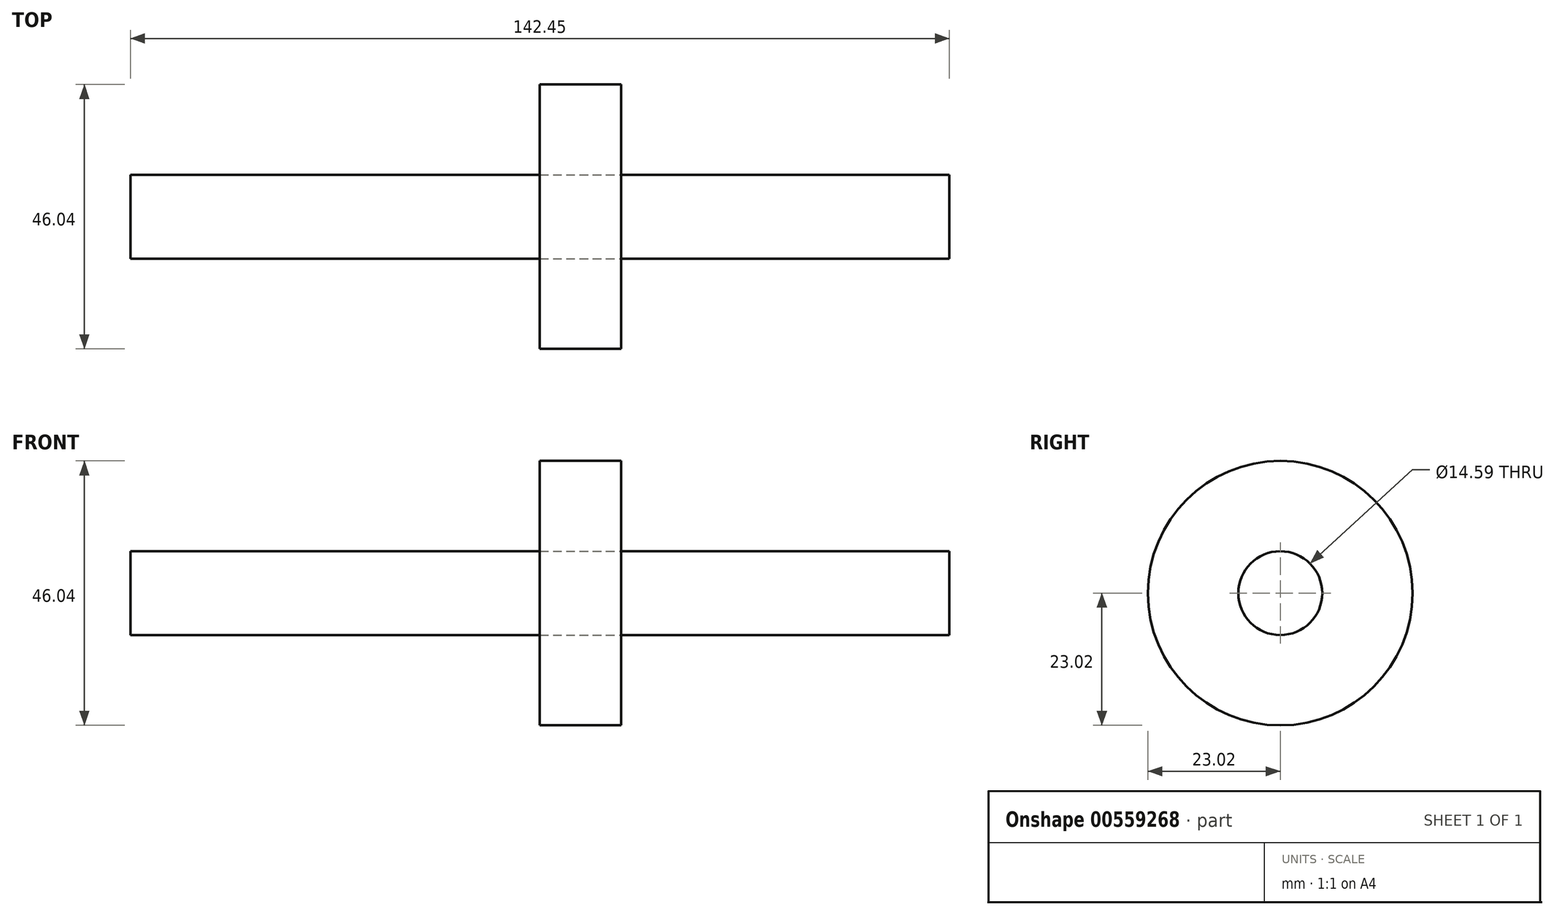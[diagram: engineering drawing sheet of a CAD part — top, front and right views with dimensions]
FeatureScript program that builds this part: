
annotation { "Feature Type Name" : "Feature", "Feature Type Description" : "" }
export const myFeature = defineFeature(function(context is Context, id is Id, definition is map)
    precondition{}
    {
        {
            var Q0;
            Q0=qCreatedBy(makeId("Front.planeOp"),FACE);
            var sketch = newSketch(context, id + "F0", { "sketchPlane" : qUnion([Q0])});
            skLineSegment(sketch, "E0.bottom", {"start": v(70.7, 7.3) * mm, "end": v(-71.75, 7.3) * mm});
            skLineSegment(sketch, "E0.top", {"start": v(70.7, 0) * mm, "end": v(-71.75, 0) * mm});
            skLineSegment(sketch, "E0.left", {"start": v(70.7, 7.3) * mm, "end": v(70.7, 0) * mm});
            skLineSegment(sketch, "E0.right", {"start": v(-71.75, 7.3) * mm, "end": v(-71.75, 0) * mm});
            skLineSegment(sketch, "E1.bottom", {"start": v(13.61, 23.02) * mm, "end": v(-0.52, 23.02) * mm});
            skLineSegment(sketch, "E1.top", {"start": v(13.61, 7.3) * mm, "end": v(-0.52, 7.3) * mm});
            skLineSegment(sketch, "E1.left", {"start": v(13.61, 23.02) * mm, "end": v(13.61, 7.3) * mm});
            skLineSegment(sketch, "E1.right", {"start": v(-0.52, 23.02) * mm, "end": v(-0.52, 7.3) * mm});
            skSolve(sketch);
        }
        {
            var Q0;
            Q0=makeQuery(id+"F0.imprint","IMPRINT",FACE,{"disambiguationData":[TD([[makeQuery(id+"F0.imprint","IMPRINT",EDGE,{"derivedFrom":sQuery(id+"F0.wireOp",EDGE,"E1.bottom")}),1.0]])]});
            var Q1;
            Q1=sQuery(id+"F0.wireOp",EDGE,"E0.top");
            revolve(context, id + "F1", {"entities" : qUnion([Q0]), "axis" : qUnion([Q1]), "revolveType" : RevolveType.FULL});
        }
        {
            var Q0;
            Q0 = qSketchRegion(id + "F0", true);
            var Q1;
            Q1=sQuery(id+"F0.wireOp",EDGE,"E0.top");
            revolve(context, id + "F2", {"entities" : qUnion([Q0]), "axis" : qUnion([Q1]), "revolveType" : RevolveType.FULL});
        }
    });
